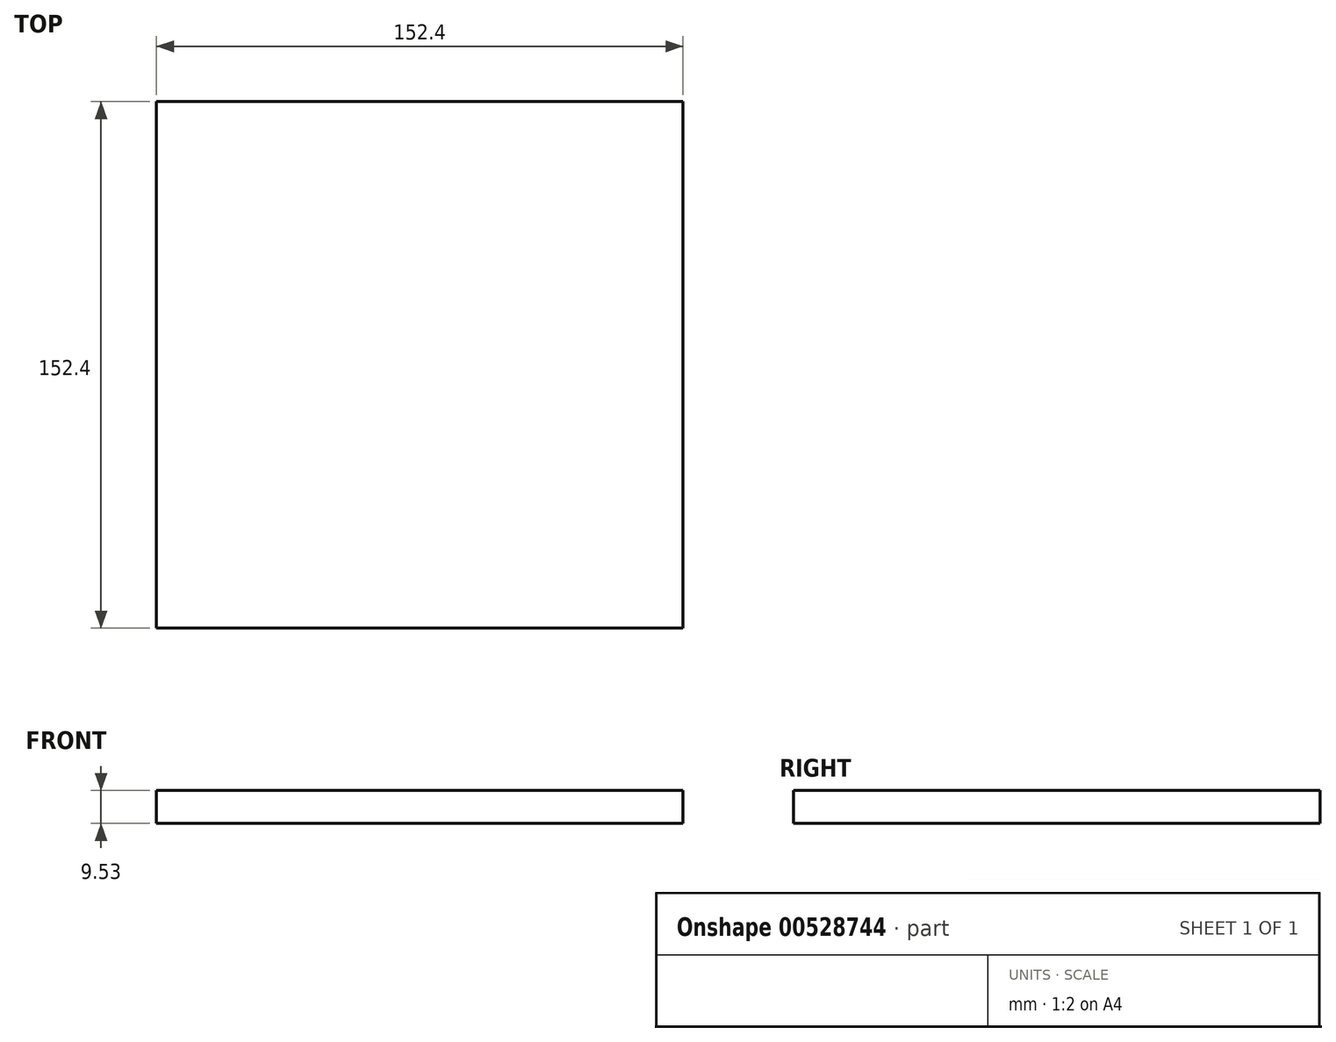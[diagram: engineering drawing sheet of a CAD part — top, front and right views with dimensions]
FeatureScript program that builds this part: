
annotation { "Feature Type Name" : "Feature", "Feature Type Description" : "" }
export const myFeature = defineFeature(function(context is Context, id is Id, definition is map)
    precondition{}
    {
        {
            var Q0;
            Q0=qCreatedBy(makeId("Top.planeOp"),FACE);
            var sketch = newSketch(context, id + "F0", { "sketchPlane" : qUnion([Q0])});
            skLineSegment(sketch, "E0.bottom", {"start": v(76.2, -76.2) * mm, "end": v(-76.2, -76.2) * mm});
            skLineSegment(sketch, "E0.top", {"start": v(76.2, 76.2) * mm, "end": v(-76.2, 76.2) * mm});
            skLineSegment(sketch, "E0.left", {"start": v(76.2, -76.2) * mm, "end": v(76.2, 76.2) * mm});
            skLineSegment(sketch, "E0.right", {"start": v(-76.2, -76.2) * mm, "end": v(-76.2, 76.2) * mm});
            skPoint(sketch, "E0.middle", {"position": v(0, 0) * mm});
            skSolve(sketch);
        }
        {
            var Q0;
            Q0 = qSketchRegion(id + "F0", true);
            extrude(context, id + "F1", {"entities" : qUnion([Q0]), "depth" : 9.52 * mm, "offsetDistance" : 25.4 * mm});
        }
    });
